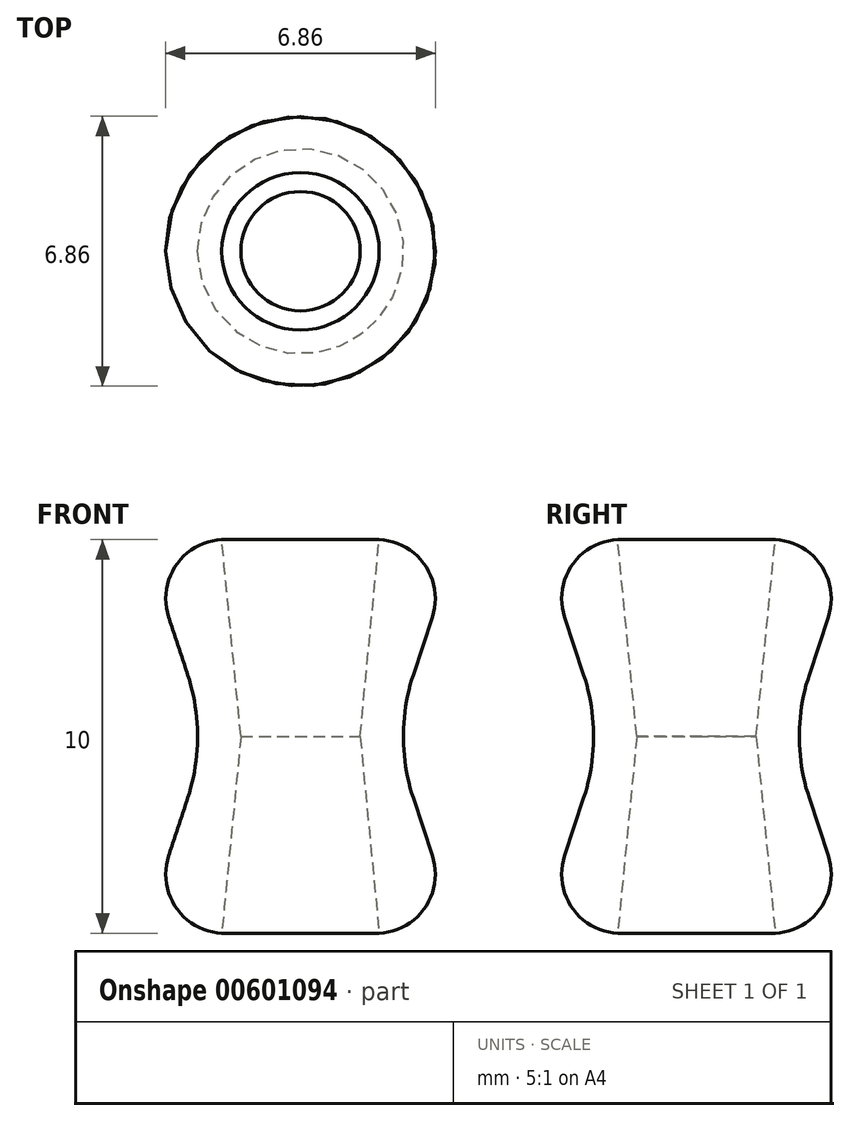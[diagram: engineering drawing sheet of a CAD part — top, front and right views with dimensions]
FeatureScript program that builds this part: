
annotation { "Feature Type Name" : "Feature", "Feature Type Description" : "" }
export const myFeature = defineFeature(function(context is Context, id is Id, definition is map)
    precondition{}
    {
        {
            var Q0;
            Q0=qCreatedBy(makeId("Front.planeOp"),FACE);
            var sketch = newSketch(context, id + "F0", { "sketchPlane" : qUnion([Q0])});
            skLineSegment(sketch, "E0", {"start": v(2, 11.24) * mm, "end": v(4, 11.24) * mm});
            skLineSegment(sketch, "E1", {"start": v(4, 11.24) * mm, "end": v(2.35, 6.24) * mm});
            skLineSegment(sketch, "E2", {"start": v(4, 1.24) * mm, "end": v(2.35, 6.24) * mm});
            skLineSegment(sketch, "E3", {"start": v(4, 1.24) * mm, "end": v(2, 1.24) * mm});
            skLineSegment(sketch, "E4", {"start": v(0, 1.24) * mm, "end": v(0, 11.24) * mm});
            skLineSegment(sketch, "E5", {"start": v(2, 11.24) * mm, "end": v(1.51, 6.24) * mm});
            skLineSegment(sketch, "E6", {"start": v(1.51, 6.24) * mm, "end": v(2, 1.24) * mm});
            skPoint(sketch, "E7", {"position": v(0, 6.24) * mm});
            skSolve(sketch);
        }
        {
            var Q0;
            {var subQ3=sQuery(id+"F0.wireOp",EDGE,"E1");Q0=makeQuery(id+"F0.imprint","IMPRINT",FACE,{"disambiguationData":[TD([[makeQuery(id+"F0.imprint","IMPRINT",EDGE,{"derivedFrom":subQ3}),-1.0]])]});}
            var Q1;
            {var subQ1=sQuery(id+"F0.wireOp",EDGE,"E4");Q1=makeQuery(id+"F0.imprint","IMPRINT",FACE,{"disambiguationData":[TD([[makeQuery(id+"F0.imprint","IMPRINT",EDGE,{"derivedFrom":subQ1}),-1.0]])]});}
            var Q2;
            Q2=sQuery(id+"F0.wireOp",EDGE,"E4");
            revolve(context, id + "F1", {"entities" : qUnion([Q0, Q1]), "axis" : qUnion([Q2]), "revolveType" : RevolveType.FULL});
        }
        {
            var Q0;
            Q0=makeQuery(id+"F1.opRevolve","SWEPT_EDGE",EDGE,{"disambiguationData":[OSD([sQuery(id+"F0.wireOp",EDGE,"E0"),sQuery(id+"F0.wireOp",EDGE,"E1")])]});
            var Q1;
            Q1=makeQuery(id+"F1.opRevolve","SWEPT_EDGE",EDGE,{"disambiguationData":[OSD([sQuery(id+"F0.wireOp",EDGE,"E2"),sQuery(id+"F0.wireOp",EDGE,"E3")])]});
            fillet(context, id + "F2", {"entities" : qUnion([Q0, Q1]), "radius" : 1.5 * mm, "tangentPropagation" : true, "allowEdgeOverflow" : false});
        }
        {
            var Q0;
            Q0=makeQuery(id+"F1.opRevolve","SWEPT_EDGE",EDGE,{"disambiguationData":[OSD([sQuery(id+"F0.wireOp",EDGE,"E1"),sQuery(id+"F0.wireOp",EDGE,"E2")])]});
            fillet(context, id + "F3", {"entities" : qUnion([Q0]), "radius" : 5 * mm, "tangentPropagation" : true, "allowEdgeOverflow" : false});
        }
    });
